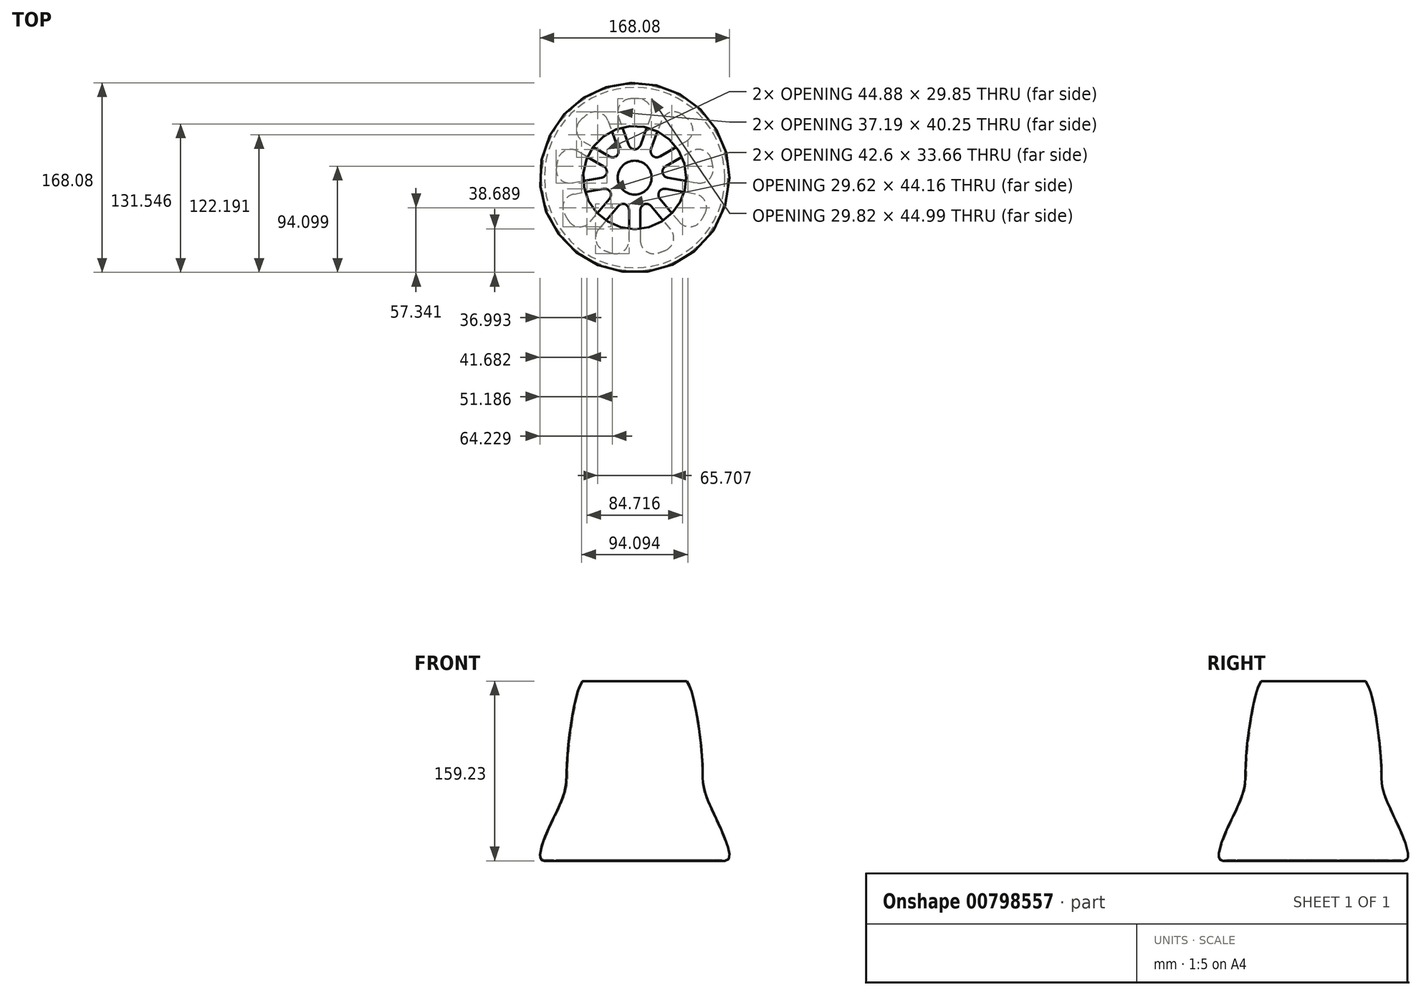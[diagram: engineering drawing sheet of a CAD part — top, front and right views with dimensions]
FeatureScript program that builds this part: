
annotation { "Feature Type Name" : "Feature", "Feature Type Description" : "" }
export const myFeature = defineFeature(function(context is Context, id is Id, definition is map)
    precondition{}
    {
        {
            var Q0;
            Q0=qCreatedBy(makeId("Top.planeOp"),FACE);
            var sketch = newSketch(context, id + "F0", { "sketchPlane" : qUnion([Q0])});
            skCircle(sketch, "E0", {"center": v(0, 0) * mm, "radius": 15 * mm});
            skCircle(sketch, "E1", {"center": v(0, 0) * mm, "radius": 80 * mm});
            skArc(sketch, "E2.0", {"start": v(5, -24.5) * mm, "mid": v(8.55, -23.5) * mm, "end": v(11.91, -21.98) * mm});
            skArc(sketch, "E3.0", {"start": v(5, -69.82) * mm, "mid": v(23.94, -65.78) * mm, "end": v(41.05, -56.7) * mm});
            skLineSegment(sketch, "E4.0", {"start": v(-5, -25) * mm, "end": v(-5, -69.82) * mm});
            skLineSegment(sketch, "E5.0", {"start": v(5, -25) * mm, "end": v(5, -70) * mm});
            skLineSegment(sketch, "E6", {"start": v(-5, -25) * mm, "end": v(-5, -24.5) * mm});
            skLineSegment(sketch, "E7", {"start": v(5, -25) * mm, "end": v(5, -24.5) * mm});
            skPoint(sketch, "E8.start.orphan", {"position": v(0, -25) * mm});
            skLineSegment(sketch, "E9.1.0", {"start": v(12.24, -22.37) * mm, "end": v(41.05, -56.7) * mm});
            skLineSegment(sketch, "E9.1.1", {"start": v(12.24, -22.37) * mm, "end": v(11.91, -21.98) * mm});
            skLineSegment(sketch, "E9.1.2", {"start": v(19.9, -15.94) * mm, "end": v(48.83, -50.4) * mm});
            skLineSegment(sketch, "E9.1.3", {"start": v(19.9, -15.94) * mm, "end": v(19.58, -15.55) * mm});
            skLineSegment(sketch, "E9.2.0", {"start": v(23.75, -9.27) * mm, "end": v(67.9, -17.05) * mm});
            skLineSegment(sketch, "E9.2.1", {"start": v(23.75, -9.27) * mm, "end": v(23.25, -9.18) * mm});
            skLineSegment(sketch, "E9.2.2", {"start": v(25.49, 0.58) * mm, "end": v(69.8, -7.23) * mm});
            skLineSegment(sketch, "E9.2.3", {"start": v(25.49, 0.58) * mm, "end": v(25, 0.67) * mm});
            skLineSegment(sketch, "E9.3.0", {"start": v(24.15, 8.17) * mm, "end": v(62.97, 30.58) * mm});
            skLineSegment(sketch, "E9.3.1", {"start": v(24.15, 8.17) * mm, "end": v(23.71, 7.92) * mm});
            skLineSegment(sketch, "E9.3.2", {"start": v(19.15, 16.83) * mm, "end": v(58.12, 39.33) * mm});
            skLineSegment(sketch, "E9.3.3", {"start": v(19.15, 16.83) * mm, "end": v(18.71, 16.58) * mm});
            skLineSegment(sketch, "E9.4.0", {"start": v(13.25, 21.78) * mm, "end": v(28.58, 63.9) * mm});
            skLineSegment(sketch, "E9.4.1", {"start": v(13.25, 21.78) * mm, "end": v(13.08, 21.3) * mm});
            skLineSegment(sketch, "E9.4.2", {"start": v(3.85, 25.2) * mm, "end": v(19.24, 67.49) * mm});
            skLineSegment(sketch, "E9.4.3", {"start": v(3.85, 25.2) * mm, "end": v(3.68, 24.73) * mm});
            skLineSegment(sketch, "E9.5.0", {"start": v(-3.85, 25.2) * mm, "end": v(-19.18, 67.32) * mm});
            skLineSegment(sketch, "E9.5.1", {"start": v(-3.85, 25.2) * mm, "end": v(-3.68, 24.73) * mm});
            skLineSegment(sketch, "E9.5.2", {"start": v(-13.25, 21.78) * mm, "end": v(-28.64, 64.07) * mm});
            skLineSegment(sketch, "E9.5.3", {"start": v(-13.25, 21.78) * mm, "end": v(-13.08, 21.3) * mm});
            skLineSegment(sketch, "E9.6.0", {"start": v(-19.15, 16.83) * mm, "end": v(-57.97, 39.24) * mm});
            skLineSegment(sketch, "E9.6.1", {"start": v(-19.15, 16.83) * mm, "end": v(-18.71, 16.58) * mm});
            skLineSegment(sketch, "E9.6.2", {"start": v(-24.15, 8.17) * mm, "end": v(-63.12, 30.67) * mm});
            skLineSegment(sketch, "E9.6.3", {"start": v(-24.15, 8.17) * mm, "end": v(-23.71, 7.92) * mm});
            skLineSegment(sketch, "E9.7.0", {"start": v(-25.49, 0.58) * mm, "end": v(-69.63, -7.2) * mm});
            skLineSegment(sketch, "E9.7.1", {"start": v(-25.49, 0.58) * mm, "end": v(-25, 0.67) * mm});
            skLineSegment(sketch, "E9.7.2", {"start": v(-23.75, -9.27) * mm, "end": v(-68.07, -17.08) * mm});
            skLineSegment(sketch, "E9.7.3", {"start": v(-23.75, -9.27) * mm, "end": v(-23.25, -9.18) * mm});
            skLineSegment(sketch, "E9.8.0", {"start": v(-19.9, -15.94) * mm, "end": v(-48.71, -50.27) * mm});
            skLineSegment(sketch, "E9.8.1", {"start": v(-19.9, -15.94) * mm, "end": v(-19.58, -15.55) * mm});
            skLineSegment(sketch, "E9.8.2", {"start": v(-12.24, -22.37) * mm, "end": v(-41.16, -56.84) * mm});
            skLineSegment(sketch, "E9.8.3", {"start": v(-12.24, -22.37) * mm, "end": v(-11.91, -21.98) * mm});
            skArc(sketch, "E10.trimOffspring", {"start": v(-41.05, -56.7) * mm, "mid": v(-23.94, -65.78) * mm, "end": v(-5, -69.82) * mm});
            skArc(sketch, "E11.trimOffspring", {"start": v(-11.91, -21.98) * mm, "mid": v(-8.55, -23.5) * mm, "end": v(-5, -24.5) * mm});
            skArc(sketch, "E12.trimOffspring", {"start": v(19.58, -15.55) * mm, "mid": v(21.65, -12.5) * mm, "end": v(23.25, -9.18) * mm});
            skArc(sketch, "E13.trimOffspring", {"start": v(48.71, -50.27) * mm, "mid": v(60.62, -35) * mm, "end": v(67.9, -17.05) * mm});
            skArc(sketch, "E14.trimOffspring", {"start": v(69.63, -7.2) * mm, "mid": v(68.94, 12.16) * mm, "end": v(62.97, 30.58) * mm});
            skArc(sketch, "E15.trimOffspring", {"start": v(25, 0.67) * mm, "mid": v(24.62, 4.34) * mm, "end": v(23.71, 7.92) * mm});
            skArc(sketch, "E16.trimOffspring", {"start": v(18.71, 16.58) * mm, "mid": v(16.07, 19.15) * mm, "end": v(13.08, 21.3) * mm});
            skArc(sketch, "E17.trimOffspring", {"start": v(57.97, 39.24) * mm, "mid": v(45, 53.62) * mm, "end": v(28.58, 63.9) * mm});
            skArc(sketch, "E18.trimOffspring", {"start": v(-23.25, -9.18) * mm, "mid": v(-21.65, -12.5) * mm, "end": v(-19.58, -15.55) * mm});
            skArc(sketch, "E19.trimOffspring", {"start": v(-67.9, -17.05) * mm, "mid": v(-60.62, -35) * mm, "end": v(-48.71, -50.27) * mm});
            skArc(sketch, "E20.trimOffspring", {"start": v(-62.97, 30.58) * mm, "mid": v(-68.94, 12.16) * mm, "end": v(-69.63, -7.2) * mm});
            skArc(sketch, "E21.trimOffspring", {"start": v(-23.71, 7.92) * mm, "mid": v(-24.62, 4.34) * mm, "end": v(-25, 0.67) * mm});
            skArc(sketch, "E22.trimOffspring", {"start": v(-13.08, 21.3) * mm, "mid": v(-16.07, 19.15) * mm, "end": v(-18.71, 16.58) * mm});
            skArc(sketch, "E23.trimOffspring", {"start": v(3.68, 24.73) * mm, "mid": v(0, 25) * mm, "end": v(-3.68, 24.73) * mm});
            skArc(sketch, "E24.trimOffspring", {"start": v(19.18, 67.32) * mm, "mid": v(0, 70) * mm, "end": v(-19.18, 67.32) * mm});
            skArc(sketch, "E25.trimOffspring", {"start": v(-28.58, 63.9) * mm, "mid": v(-45, 53.62) * mm, "end": v(-57.97, 39.24) * mm});
            skSolve(sketch);
        }
        {
            var Q0;
            Q0 = qSketchRegion(id + "F0", true);
            extrude(context, id + "F1", {"entities" : qUnion([Q0]), "depth" : 0.8 * mm, "offsetDistance" : 25 * mm});
        }
        {
            var Q0;
            Q0=qCreatedBy(makeId("Front.planeOp"),FACE);
            var sketch = newSketch(context, id + "F2", { "sketchPlane" : qUnion([Q0])});
            skFitSpline(sketch, "E26", {"points": [v(80, 0) * mm, v(65, 53.27) * mm, v(60, 88.07) * mm, v(45, 160) * mm], "startDerivative": vector(110.9, 1.25) * mm, "endDerivative": vector(-52.8, 11.7) * mm});
            skFitSpline(sketch, "E27.0", {"points": [v(80, 0.8) * mm, v(80.5, 0.8) * mm, v(81.14, 0.91) * mm, v(81.77, 1.2) * mm, v(82.15, 1.47) * mm, v(82.48, 1.82) * mm, v(82.84, 2.4) * mm, v(83.15, 3.37) * mm, v(83.28, 4.93) * mm, v(83.14, 6.83) * mm, v(82.75, 9.02) * mm, v(81.91, 12.27) * mm, v(80.36, 16.88) * mm, v(77.9, 23) * mm, v(75.03, 29.45) * mm, v(71.98, 36.01) * mm, v(68.96, 42.42) * mm, v(66.64, 47.45) * mm, v(65.01, 51.16) * mm, v(63.93, 53.76) * mm, v(63, 56.16) * mm, v(61.95, 59.13) * mm, v(60.96, 62.47) * mm, v(60.2, 66.1) * mm, v(59.77, 69.53) * mm, v(59.58, 72.96) * mm, v(59.5, 76.59) * mm, v(59.47, 79.95) * mm, v(59.4, 82.94) * mm, v(59.33, 85.37) * mm, v(59.2, 88) * mm, v(59.04, 90.86) * mm, v(58.8, 93.94) * mm, v(58.44, 98.28) * mm, v(57.86, 104.1) * mm, v(57, 111.47) * mm, v(55.97, 119.02) * mm, v(54.8, 126.54) * mm, v(53.52, 133.8) * mm, v(52.13, 140.6) * mm, v(50.66, 146.7) * mm, v(49.38, 151.02) * mm, v(48.34, 153.9) * mm, v(47.55, 155.75) * mm, v(46.77, 157.25) * mm, v(46.02, 158.36) * mm, v(45.44, 158.92) * mm, v(45.06, 159.15) * mm, v(44.9, 159.2) * mm, v(44.83, 159.22) * mm]});
            skLineSegment(sketch, "E28", {"start": v(45, 160) * mm, "end": v(46.19, 158.08) * mm});
            skLineSegment(sketch, "E29", {"start": v(80, 0) * mm, "end": v(80, 0.8) * mm});
            skLineSegment(sketch, "E30", {"start": v(0, 0) * mm, "end": v(0, 21.91) * mm, "construction": true});
            skSolve(sketch);
        }
        {
            var Q0;
            Q0 = qSketchRegion(id + "F2", true);
            var Q1;
            Q1=sQuery(id+"F2.wireOp",EDGE,"E30");
            revolve(context, id + "F3", {"operationType" : NewBodyOperationType.ADD, "surfaceOperationType" : NewSurfaceOperationType.NEW, "entities" : qUnion([Q0]), "axis" : qUnion([Q1]), "revolveType" : RevolveType.FULL});
        }
        {
            var Q0;
            Q0=makeQuery(id+"F1.opExtrude","SWEPT_EDGE",EDGE,{"disambiguationData":[OSD([sQuery(id+"F0.wireOp",EDGE,"E9.8.1"),sQuery(id+"F0.wireOp",EDGE,"E18.trimOffspring")])]});
            var Q1;
            Q1=makeQuery(id+"F1.opExtrude","SWEPT_EDGE",EDGE,{"disambiguationData":[OSD([sQuery(id+"F0.wireOp",EDGE,"E6"),sQuery(id+"F0.wireOp",EDGE,"E11.trimOffspring")])]});
            var Q2;
            Q2=makeQuery(id+"F1.opExtrude","SWEPT_EDGE",EDGE,{"disambiguationData":[OSD([sQuery(id+"F0.wireOp",EDGE,"E2.0"),sQuery(id+"F0.wireOp",EDGE,"E9.1.1")])]});
            var Q3;
            Q3=makeQuery(id+"F1.opExtrude","SWEPT_EDGE",EDGE,{"disambiguationData":[OSD([sQuery(id+"F0.wireOp",EDGE,"E9.2.1"),sQuery(id+"F0.wireOp",EDGE,"E12.trimOffspring")])]});
            var Q4;
            Q4=makeQuery(id+"F1.opExtrude","SWEPT_EDGE",EDGE,{"disambiguationData":[OSD([sQuery(id+"F0.wireOp",EDGE,"E9.3.1"),sQuery(id+"F0.wireOp",EDGE,"E15.trimOffspring")])]});
            var Q5;
            Q5=makeQuery(id+"F1.opExtrude","SWEPT_EDGE",EDGE,{"disambiguationData":[OSD([sQuery(id+"F0.wireOp",EDGE,"E9.4.1"),sQuery(id+"F0.wireOp",EDGE,"E16.trimOffspring")])]});
            var Q6;
            Q6=makeQuery(id+"F1.opExtrude","SWEPT_EDGE",EDGE,{"disambiguationData":[OSD([sQuery(id+"F0.wireOp",EDGE,"E9.3.3"),sQuery(id+"F0.wireOp",EDGE,"E16.trimOffspring")])]});
            var Q7;
            Q7=makeQuery(id+"F1.opExtrude","SWEPT_EDGE",EDGE,{"disambiguationData":[OSD([sQuery(id+"F0.wireOp",EDGE,"E9.2.3"),sQuery(id+"F0.wireOp",EDGE,"E15.trimOffspring")])]});
            var Q8;
            Q8=makeQuery(id+"F1.opExtrude","SWEPT_EDGE",EDGE,{"disambiguationData":[OSD([sQuery(id+"F0.wireOp",EDGE,"E9.1.3"),sQuery(id+"F0.wireOp",EDGE,"E12.trimOffspring")])]});
            var Q9;
            Q9=makeQuery(id+"F1.opExtrude","SWEPT_EDGE",EDGE,{"disambiguationData":[OSD([sQuery(id+"F0.wireOp",EDGE,"E2.0"),sQuery(id+"F0.wireOp",EDGE,"E7")])]});
            var Q10;
            Q10=makeQuery(id+"F1.opExtrude","SWEPT_EDGE",EDGE,{"disambiguationData":[OSD([sQuery(id+"F0.wireOp",EDGE,"E9.8.3"),sQuery(id+"F0.wireOp",EDGE,"E11.trimOffspring")])]});
            var Q11;
            Q11=makeQuery(id+"F1.opExtrude","SWEPT_EDGE",EDGE,{"disambiguationData":[OSD([sQuery(id+"F0.wireOp",EDGE,"E9.7.3"),sQuery(id+"F0.wireOp",EDGE,"E18.trimOffspring")])]});
            var Q12;
            Q12=makeQuery(id+"F1.opExtrude","SWEPT_EDGE",EDGE,{"disambiguationData":[OSD([sQuery(id+"F0.wireOp",EDGE,"E9.7.1"),sQuery(id+"F0.wireOp",EDGE,"E21.trimOffspring")])]});
            var Q13;
            Q13=makeQuery(id+"F1.opExtrude","SWEPT_EDGE",EDGE,{"disambiguationData":[OSD([sQuery(id+"F0.wireOp",EDGE,"E9.6.3"),sQuery(id+"F0.wireOp",EDGE,"E21.trimOffspring")])]});
            var Q14;
            Q14=makeQuery(id+"F1.opExtrude","SWEPT_EDGE",EDGE,{"disambiguationData":[OSD([sQuery(id+"F0.wireOp",EDGE,"E9.6.1"),sQuery(id+"F0.wireOp",EDGE,"E22.trimOffspring")])]});
            var Q15;
            Q15=makeQuery(id+"F1.opExtrude","SWEPT_EDGE",EDGE,{"disambiguationData":[OSD([sQuery(id+"F0.wireOp",EDGE,"E9.5.3"),sQuery(id+"F0.wireOp",EDGE,"E22.trimOffspring")])]});
            var Q16;
            Q16=makeQuery(id+"F1.opExtrude","SWEPT_EDGE",EDGE,{"disambiguationData":[OSD([sQuery(id+"F0.wireOp",EDGE,"E9.4.3"),sQuery(id+"F0.wireOp",EDGE,"E23.trimOffspring")])]});
            var Q17;
            Q17=makeQuery(id+"F1.opExtrude","SWEPT_EDGE",EDGE,{"disambiguationData":[OSD([sQuery(id+"F0.wireOp",EDGE,"E9.5.1"),sQuery(id+"F0.wireOp",EDGE,"E23.trimOffspring")])]});
            fillet(context, id + "F4", {"entities" : qUnion([Q0, Q1, Q2, Q3, Q4, Q5, Q6, Q7, Q8, Q9, Q10, Q11, Q12, Q13, Q14, Q15, Q16, Q17]), "radius" : 6 * mm, "tangentPropagation" : true, "allowEdgeOverflow" : false});
        }
        {
            var Q0;
            Q0=makeQuery(id+"F1.opExtrude","SWEPT_EDGE",EDGE,{"disambiguationData":[OSD([sQuery(id+"F0.wireOp",EDGE,"E9.7.0"),sQuery(id+"F0.wireOp",EDGE,"E20.trimOffspring")])]});
            var Q1;
            Q1=makeQuery(id+"F1.opExtrude","SWEPT_EDGE",EDGE,{"disambiguationData":[OSD([sQuery(id+"F0.wireOp",EDGE,"E9.7.2"),sQuery(id+"F0.wireOp",EDGE,"E19.trimOffspring")])]});
            var Q2;
            Q2=makeQuery(id+"F1.opExtrude","SWEPT_EDGE",EDGE,{"disambiguationData":[OSD([sQuery(id+"F0.wireOp",EDGE,"E9.8.0"),sQuery(id+"F0.wireOp",EDGE,"E19.trimOffspring")])]});
            var Q3;
            Q3=makeQuery(id+"F1.opExtrude","SWEPT_EDGE",EDGE,{"disambiguationData":[OSD([sQuery(id+"F0.wireOp",EDGE,"E9.8.2"),sQuery(id+"F0.wireOp",EDGE,"E10.trimOffspring")])]});
            var Q4;
            Q4=makeQuery(id+"F1.opExtrude","SWEPT_EDGE",EDGE,{"disambiguationData":[OSD([sQuery(id+"F0.wireOp",EDGE,"E4.0"),sQuery(id+"F0.wireOp",EDGE,"E10.trimOffspring")])]});
            var Q5;
            Q5=makeQuery(id+"F1.opExtrude","SWEPT_EDGE",EDGE,{"disambiguationData":[OSD([sQuery(id+"F0.wireOp",EDGE,"E3.0"),sQuery(id+"F0.wireOp",EDGE,"E5.0")])]});
            var Q6;
            Q6=makeQuery(id+"F1.opExtrude","SWEPT_EDGE",EDGE,{"disambiguationData":[OSD([sQuery(id+"F0.wireOp",EDGE,"E3.0"),sQuery(id+"F0.wireOp",EDGE,"E9.1.0")])]});
            var Q7;
            Q7=makeQuery(id+"F1.opExtrude","SWEPT_EDGE",EDGE,{"disambiguationData":[OSD([sQuery(id+"F0.wireOp",EDGE,"E9.1.2"),sQuery(id+"F0.wireOp",EDGE,"E13.trimOffspring")])]});
            var Q8;
            Q8=makeQuery(id+"F1.opExtrude","SWEPT_EDGE",EDGE,{"disambiguationData":[OSD([sQuery(id+"F0.wireOp",EDGE,"E9.2.0"),sQuery(id+"F0.wireOp",EDGE,"E13.trimOffspring")])]});
            var Q9;
            Q9=makeQuery(id+"F1.opExtrude","SWEPT_EDGE",EDGE,{"disambiguationData":[OSD([sQuery(id+"F0.wireOp",EDGE,"E9.2.2"),sQuery(id+"F0.wireOp",EDGE,"E14.trimOffspring")])]});
            var Q10;
            Q10=makeQuery(id+"F1.opExtrude","SWEPT_EDGE",EDGE,{"disambiguationData":[OSD([sQuery(id+"F0.wireOp",EDGE,"E9.3.0"),sQuery(id+"F0.wireOp",EDGE,"E14.trimOffspring")])]});
            var Q11;
            Q11=makeQuery(id+"F1.opExtrude","SWEPT_EDGE",EDGE,{"disambiguationData":[OSD([sQuery(id+"F0.wireOp",EDGE,"E9.3.2"),sQuery(id+"F0.wireOp",EDGE,"E17.trimOffspring")])]});
            var Q12;
            Q12=makeQuery(id+"F1.opExtrude","SWEPT_EDGE",EDGE,{"disambiguationData":[OSD([sQuery(id+"F0.wireOp",EDGE,"E9.4.0"),sQuery(id+"F0.wireOp",EDGE,"E17.trimOffspring")])]});
            var Q13;
            Q13=makeQuery(id+"F1.opExtrude","SWEPT_EDGE",EDGE,{"disambiguationData":[OSD([sQuery(id+"F0.wireOp",EDGE,"E9.4.2"),sQuery(id+"F0.wireOp",EDGE,"E24.trimOffspring")])]});
            var Q14;
            Q14=makeQuery(id+"F1.opExtrude","SWEPT_EDGE",EDGE,{"disambiguationData":[OSD([sQuery(id+"F0.wireOp",EDGE,"E9.5.0"),sQuery(id+"F0.wireOp",EDGE,"E24.trimOffspring")])]});
            var Q15;
            Q15=makeQuery(id+"F1.opExtrude","SWEPT_EDGE",EDGE,{"disambiguationData":[OSD([sQuery(id+"F0.wireOp",EDGE,"E9.5.2"),sQuery(id+"F0.wireOp",EDGE,"E25.trimOffspring")])]});
            var Q16;
            Q16=makeQuery(id+"F1.opExtrude","SWEPT_EDGE",EDGE,{"disambiguationData":[OSD([sQuery(id+"F0.wireOp",EDGE,"E9.6.0"),sQuery(id+"F0.wireOp",EDGE,"E25.trimOffspring")])]});
            var Q17;
            Q17=makeQuery(id+"F1.opExtrude","SWEPT_EDGE",EDGE,{"disambiguationData":[OSD([sQuery(id+"F0.wireOp",EDGE,"E9.6.2"),sQuery(id+"F0.wireOp",EDGE,"E20.trimOffspring")])]});
            fillet(context, id + "F5", {"entities" : qUnion([Q0, Q1, Q2, Q3, Q4, Q5, Q6, Q7, Q8, Q9, Q10, Q11, Q12, Q13, Q14, Q15, Q16, Q17]), "radius" : 12 * mm, "tangentPropagation" : true, "allowEdgeOverflow" : false});
        }
        {
            var Q0;
            Q0=makeQuery(id+"F3.opRevolve","SWEPT_EDGE",EDGE,{"disambiguationData":[OSD([sQuery(id+"F2.wireOp",EDGE,"E26"),sQuery(id+"F2.wireOp",EDGE,"E28")])]});
            var Q1;
            Q1=makeQuery(id+"F3.opRevolve","SWEPT_EDGE",EDGE,{"disambiguationData":[OSD([sQuery(id+"F2.wireOp",EDGE,"E27.0"),sQuery(id+"F2.wireOp",EDGE,"E28")])]});
            fillet(context, id + "F6", {"entities" : qUnion([Q0, Q1]), "radius" : 0.35 * mm, "tangentPropagation" : true, "allowEdgeOverflow" : false});
        }
    });
